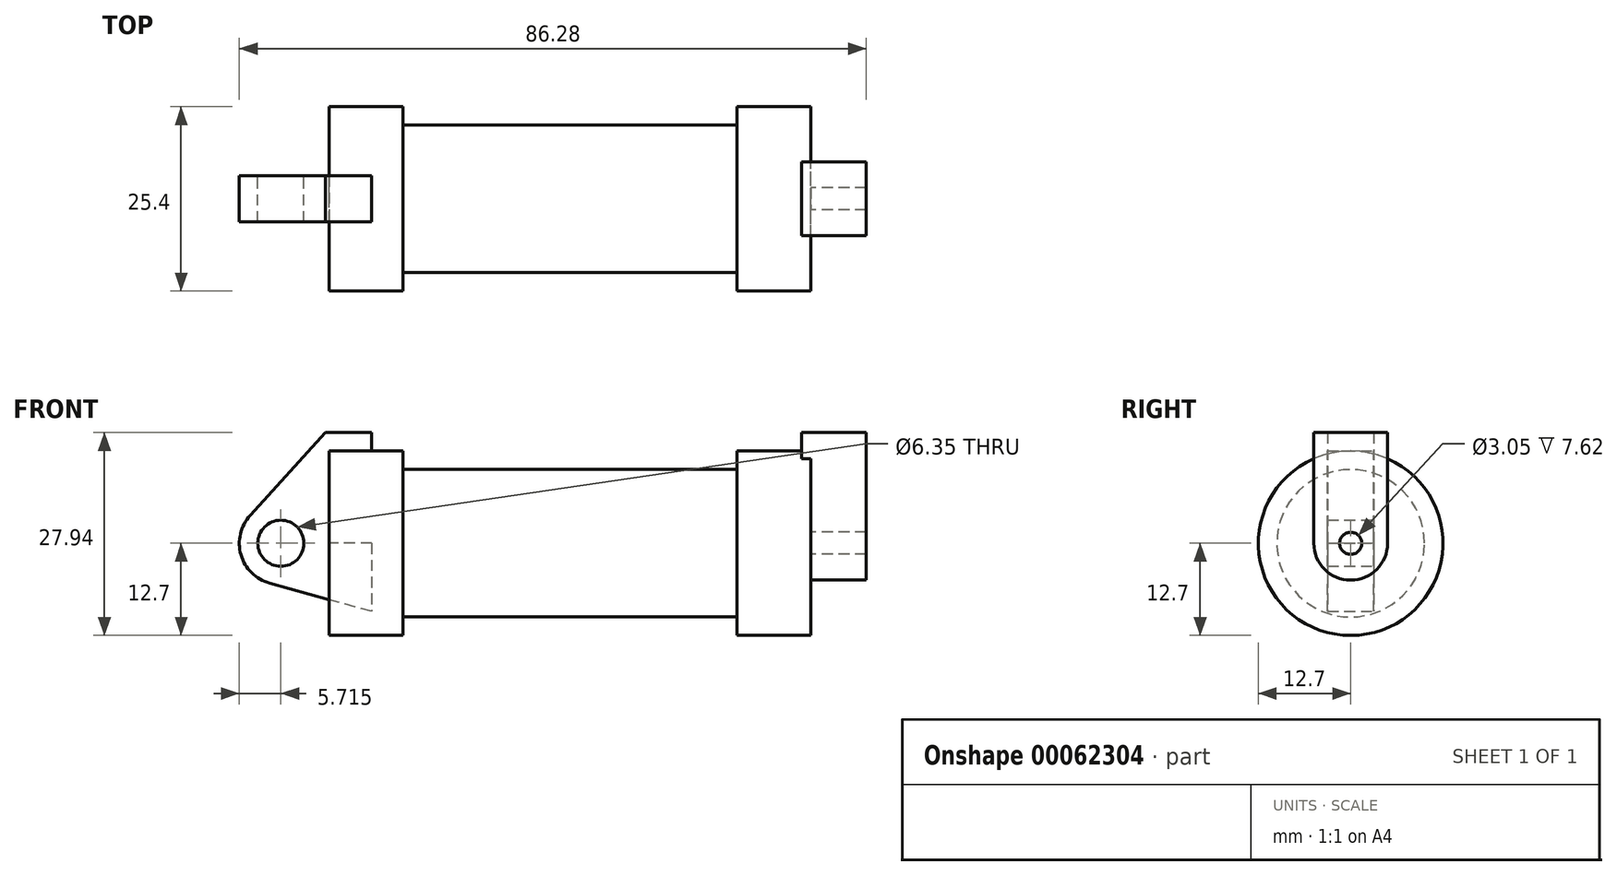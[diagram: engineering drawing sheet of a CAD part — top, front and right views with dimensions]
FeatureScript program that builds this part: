
annotation { "Feature Type Name" : "Feature", "Feature Type Description" : "" }
export const myFeature = defineFeature(function(context is Context, id is Id, definition is map)
    precondition{}
    {
        {
            var Q0;
            Q0=qCreatedBy(makeId("Front.planeOp"),FACE);
            var sketch = newSketch(context, id + "F0", { "sketchPlane" : qUnion([Q0])});
            skLineSegment(sketch, "E0", {"start": v(0, 0) * mm, "end": v(0, 12.7) * mm});
            skLineSegment(sketch, "E1", {"start": v(0, 12.7) * mm, "end": v(10.16, 12.7) * mm});
            skLineSegment(sketch, "E2", {"start": v(10.16, 12.7) * mm, "end": v(10.16, 10.16) * mm});
            skLineSegment(sketch, "E3", {"start": v(10.16, 10.16) * mm, "end": v(56.13, 10.16) * mm});
            skLineSegment(sketch, "E4", {"start": v(56.13, 10.16) * mm, "end": v(56.13, 12.7) * mm});
            skLineSegment(sketch, "E5", {"start": v(56.13, 12.7) * mm, "end": v(66.3, 12.7) * mm});
            skLineSegment(sketch, "E6", {"start": v(66.3, 12.7) * mm, "end": v(66.3, 0) * mm});
            skLineSegment(sketch, "E7", {"start": v(66.3, 0) * mm, "end": v(0, 0) * mm});
            skLineSegment(sketch, "E8", {"start": v(5.84, 15.24) * mm, "end": v(-0.5, 15.24) * mm});
            skLineSegment(sketch, "E9", {"start": v(-0.5, 15.24) * mm, "end": v(-10.88, 3.85) * mm});
            skLineSegment(sketch, "E10", {"start": v(0, 0) * mm, "end": v(-6.65, 0) * mm});
            skCircle(sketch, "E11", {"center": v(-6.65, 0) * mm, "radius": 5.72 * mm});
            skCircle(sketch, "E12", {"center": v(-6.65, 0) * mm, "radius": 3.18 * mm});
            skLineSegment(sketch, "E13", {"start": v(5.84, 15.24) * mm, "end": v(5.84, -9.4) * mm});
            skLineSegment(sketch, "E14", {"start": v(5.84, -9.4) * mm, "end": v(-8.18, -5.5) * mm});
            skSolve(sketch);
        }
        {
            var Q0;
            {var subQ0=sQuery(id+"F0.wireOp",EDGE,"E0");Q0=makeQuery(id+"F0.imprint","IMPRINT",FACE,{"disambiguationData":[TD([[makeQuery(id+"F0.imprint","IMPRINT",EDGE,{"derivedFrom":subQ0}),-1.0]])]});}
            var Q1;
            {var subQ0=sQuery(id+"F0.wireOp",EDGE,"E2");Q1=makeQuery(id+"F0.imprint","IMPRINT",FACE,{"disambiguationData":[TD([[makeQuery(id+"F0.imprint","IMPRINT",EDGE,{"derivedFrom":subQ0}),-1.0]])]});}
            var Q2;
            Q2=sQuery(id+"F0.wireOp",EDGE,"E7");
            revolve(context, id + "F1", {"entities" : qUnion([Q0, Q1]), "axis" : qUnion([Q2]), "revolveType" : RevolveType.FULL});
        }
        {
            var Q0;
            {var subQ3=sQuery(id+"F0.wireOp",EDGE,"E0");Q0=makeQuery(id+"F0.imprint","IMPRINT",FACE,{"disambiguationData":[TD([[makeQuery(id+"F0.imprint","IMPRINT",EDGE,{"derivedFrom":subQ3}),1.0]])]});}
            var Q1;
            {var subQ4=sQuery(id+"F0.wireOp",EDGE,"E12");Q1=makeQuery(id+"F0.imprint","IMPRINT",FACE,{"disambiguationData":[TD([[makeQuery(id+"F0.imprint","IMPRINT",EDGE,{"derivedFrom":subQ4}),-1.0]])]});}
            var Q2;
            {var subQ0=sQuery(id+"F0.wireOp",EDGE,"E14");Q2=makeQuery(id+"F0.imprint","IMPRINT",FACE,{"disambiguationData":[TD([[makeQuery(id+"F0.imprint","IMPRINT",EDGE,{"derivedFrom":subQ0}),-1.0]])]});}
            extrude(context, id + "F2", {"entities" : qUnion([Q0, Q1, Q2]), "endBound" : BoundingType.SYMMETRIC, "depth" : 6.35 * mm});
        }
        {
            var Q0;
            Q0=makeQuery(id+"F1.opRevolve","SWEPT_FACE",FACE,{"disambiguationData":[OSD([sQuery(id+"F0.wireOp",EDGE,"E6")])]});
            var sketch = newSketch(context, id + "F3", { "sketchPlane" : qUnion([Q0])});
            skCircle(sketch, "E15", {"center": v(0, 0) * mm, "radius": 5.08 * mm});
            skCircle(sketch, "E16", {"center": v(0, 0) * mm, "radius": 1.52 * mm});
            skLineSegment(sketch, "E17", {"start": v(5.08, 15.24) * mm, "end": v(-5.08, 15.24) * mm});
            skLineSegment(sketch, "E18", {"start": v(-5.08, 15.24) * mm, "end": v(-5.08, 0) * mm});
            skLineSegment(sketch, "E19", {"start": v(5.08, 15.24) * mm, "end": v(5.08, 0) * mm});
            skSolve(sketch);
        }
        {
            var Q0;
            Q0 = qSketchRegion(id + "F3", true);
            extrude(context, id + "F4", {"entities" : qUnion([Q0]), "operationType" : NewBodyOperationType.ADD, "depth" : 7.62 * mm});
        }
        {
            var Q0;
            Q0 = qSketchRegion(id + "F3", true);
            extrude(context, id + "F5", {"entities" : qUnion([Q0]), "operationType" : NewBodyOperationType.ADD, "oppositeDirection" : true, "depth" : 1.27 * mm});
        }
    });
